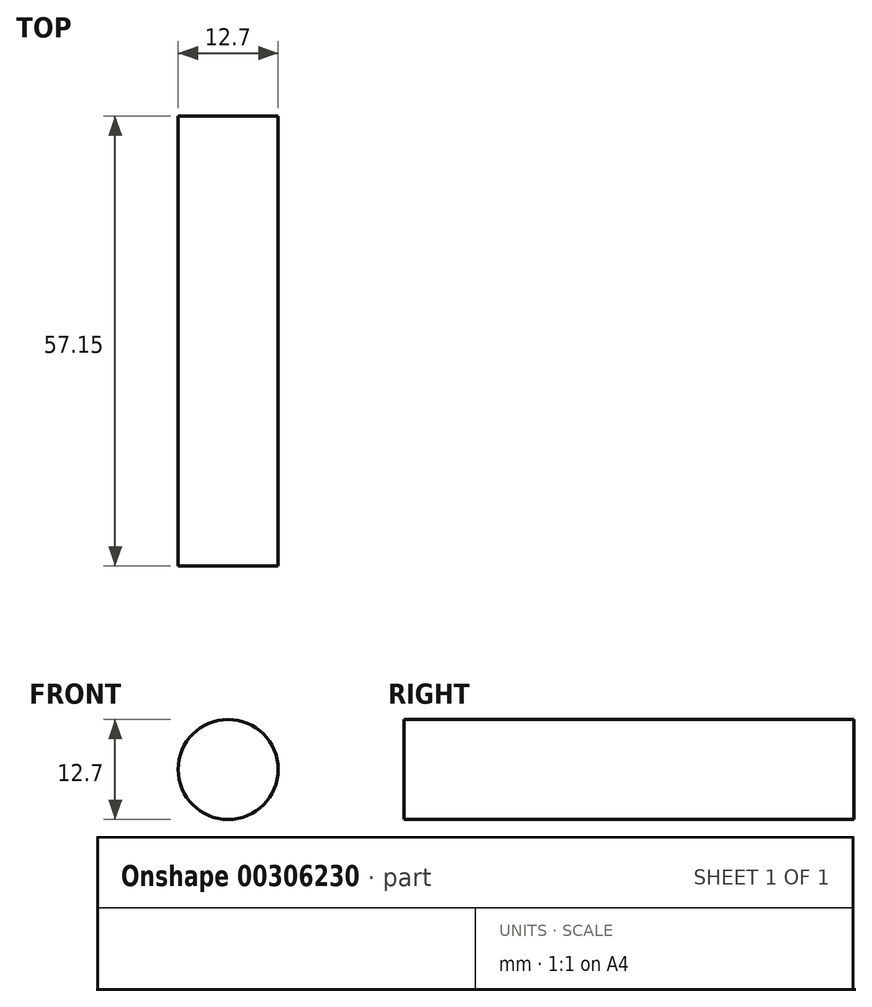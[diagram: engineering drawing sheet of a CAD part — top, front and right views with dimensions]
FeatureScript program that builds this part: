
annotation { "Feature Type Name" : "Feature", "Feature Type Description" : "" }
export const myFeature = defineFeature(function(context is Context, id is Id, definition is map)
    precondition{}
    {
        {
            var Q0;
            Q0=qCreatedBy(makeId("Front.planeOp"),FACE);
            var sketch = newSketch(context, id + "F0", { "sketchPlane" : qUnion([Q0])});
            skCircle(sketch, "E0", {"center": v(0, 0) * mm, "radius": 6.35 * mm});
            skSolve(sketch);
        }
        {
            var Q0;
            Q0 = qSketchRegion(id + "F0", true);
            extrude(context, id + "F1", {"entities" : qUnion([Q0]), "depth" : 57.15 * mm});
        }
    });
